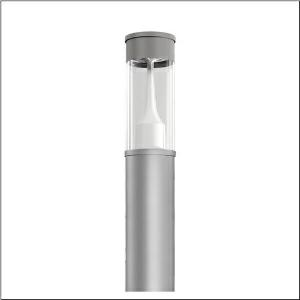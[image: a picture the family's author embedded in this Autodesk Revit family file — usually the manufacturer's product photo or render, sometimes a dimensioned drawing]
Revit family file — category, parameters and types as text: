
# Revit family: city-light_400_iq___p1_0a_5xa5305bf14hp_df67
name_source: partatom
category: Lighting Fixtures
units: mm (PartAtom-declared; Revit-internal decimal feet)

## family parameters
Cut with Voids When Loaded = No
Host = Face
Light Source = No
Part Type = Normal
Room Calculation Point = No
Round Connector Dimension = Use Diameter
Shared = No

## types (1)
- --- (1 x LED, 3890 lm, 33.6 W, 2200K)
    Apparent Load = 34 VA
    CIE Flux Codes = 31 62 91 95 100
    Color Rendering = 70
    Color Temperature = 2200K
    Default Elevation = 1800 mm
    Description = City-Light 400 iQ, light pillar, Module 540 iQ-SR, primary light control with 3 zone facetted reflector, of plastic, silver coated, highly specular, structured, primary optical cover: cover, of PMMA, transparent, partly coated, light distribution: P1.0a, primary light characteristic: strongly asymmetric, LED, High Power LED, rated luminous flux: 3.890lm, luminous efficacy: 116lm/W, light colour: 722, colour temperature: 2200K, control gear: ECG iQ, control: presetting dimming logarithmic, Street-Remote, Auto-Match, Temp-Guard, Lumen-Switch, Night-Set, Smart-Wire, Light-Fading, Desk-Remote (wireless, voltage-free reading and setting of iQ features in the workshop via application-optimized NFC function/RFID function), optimised constant luminous flux control (CLO 2.0), with terminal, 6-pole, max. 2.5mm², mains connection: 230..240V, AC, 50/60Hz, start of lifetime: 34W, end of service life: 36W, reduction: 15W, luminaire housing, cylindrical, of extruded aluminium section, coated, Siteco® metallic grey (DB 702S), length: 4.694mm, diameter: 200mm, Module 540 iQ-SR, traffic white (RAL 9016), equipment: Power, protection rating (complete): IP65, insulation class (complete): insulation class II (safety insulation), certification: CE, ENEC, VDE, packaging unit: 1 piece

Light Distribution: P1.0a
    Height = 500 mm
    Lamp = 1 x LED
    Lamp Light Flux = 3890 lm
    Lamp Power = 33.6 W
    Lamp count = 1
    Length = 200 mm  [stored 0.656168 ft]
    Luminous efficacy = 116 lm/W
    Manufacturer = Siteco
    ModVariant = No
    Model = 5XA5305BF14HP
    Mounting Place = Floor
    Mounting Type = Freestanding
    Number of Poles = 1
    OnlyDefault = Yes
    Power Factor = 1
    Product Name = City-Light 400 iQ | P1.0a
    Product group = light pillar
    ProductGroupID = 1303
    Protection Class = Protection class II
    Protection Degree = IP 65
    RLX_Detail_Level = 1
    RLX_Emergency_Light_Flux = 0 lm
    RLX_Emergency_Type = 0
    RLX_Emergency_Type_DB = No
    RlxData = <blob elided: 53409 chars, md5=595e211f>
    Socket = socket
    Standby Power = 0 W
    System Light Flux = 3890 lm
    System Power = 34 W
    Type Comments = factory setting: luminous flux: 100 % | dim-lin: 254 | 695 mA
    Type Image = l_1006916.jpg
    URL = http://relux.com
    VarID = @adj_127221
    Voltage = 0 V
    Weight = 0.00 kg
    Width = 0 mm  [stored 0 ft]

note: [stored X ft] marks values corroborated as IEEE doubles in the binary element streams (Revit-internal decimal feet)

## geometry (parser evidence)
native form markers: Blend x4, Sweep x12
no freeform markers — native parametric forms only
